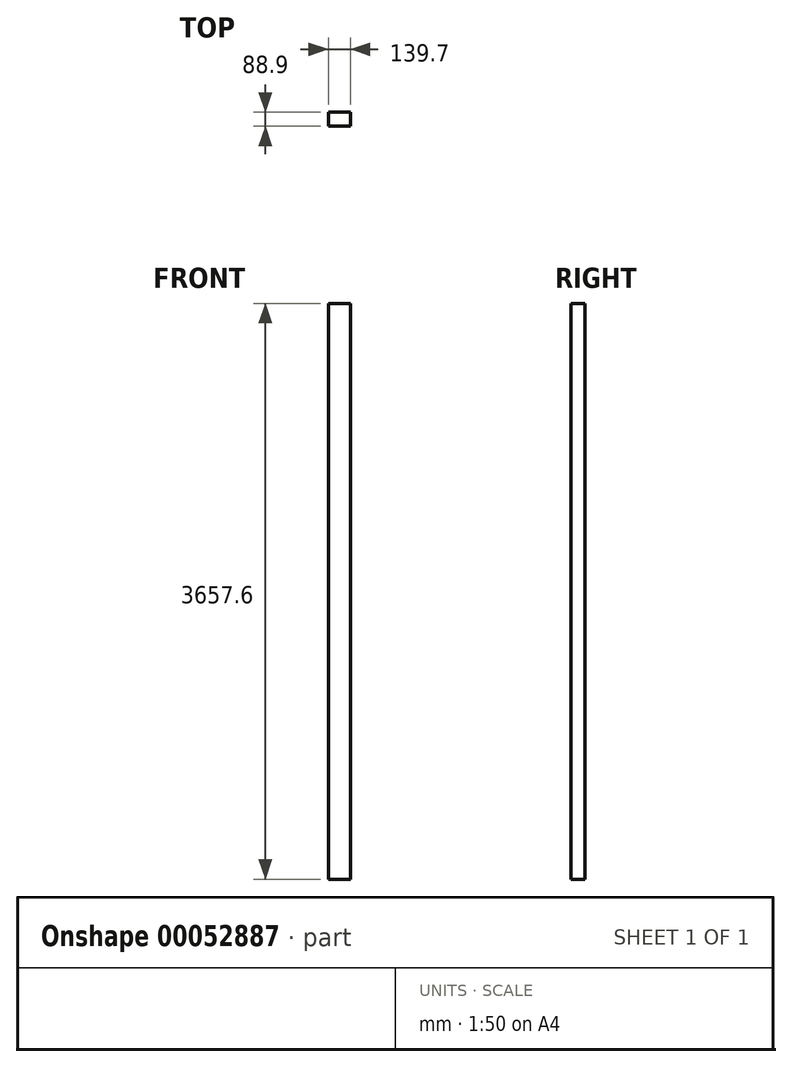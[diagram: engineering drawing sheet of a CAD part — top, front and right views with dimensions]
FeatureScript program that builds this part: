
annotation { "Feature Type Name" : "Feature", "Feature Type Description" : "" }
export const myFeature = defineFeature(function(context is Context, id is Id, definition is map)
    precondition{}
    {
        {
            var Q0;
            Q0=qCreatedBy(makeId("Top.planeOp"),FACE);
            var sketch = newSketch(context, id + "F0", { "sketchPlane" : qUnion([Q0])});
            skLineSegment(sketch, "E0.bottom", {"start": v(0, 0) * mm, "end": v(139.7, 0) * mm});
            skLineSegment(sketch, "E0.top", {"start": v(0, 88.9) * mm, "end": v(139.7, 88.9) * mm});
            skLineSegment(sketch, "E0.left", {"start": v(0, 0) * mm, "end": v(0, 88.9) * mm});
            skLineSegment(sketch, "E0.right", {"start": v(139.7, 0) * mm, "end": v(139.7, 88.9) * mm});
            skSolve(sketch);
        }
        {
            var Q0;
            Q0=makeQuery(id+"F0.imprint","IMPRINT",FACE,{"disambiguationData":[TD([[makeQuery(id+"F0.imprint","IMPRINT",EDGE,{"derivedFrom":sQuery(id+"F0.wireOp",EDGE,"E0.bottom")}),1.0]])]});
            extrude(context, id + "F1", {"entities" : qUnion([Q0]), "depth" : 3657.6 * mm});
        }
    });
